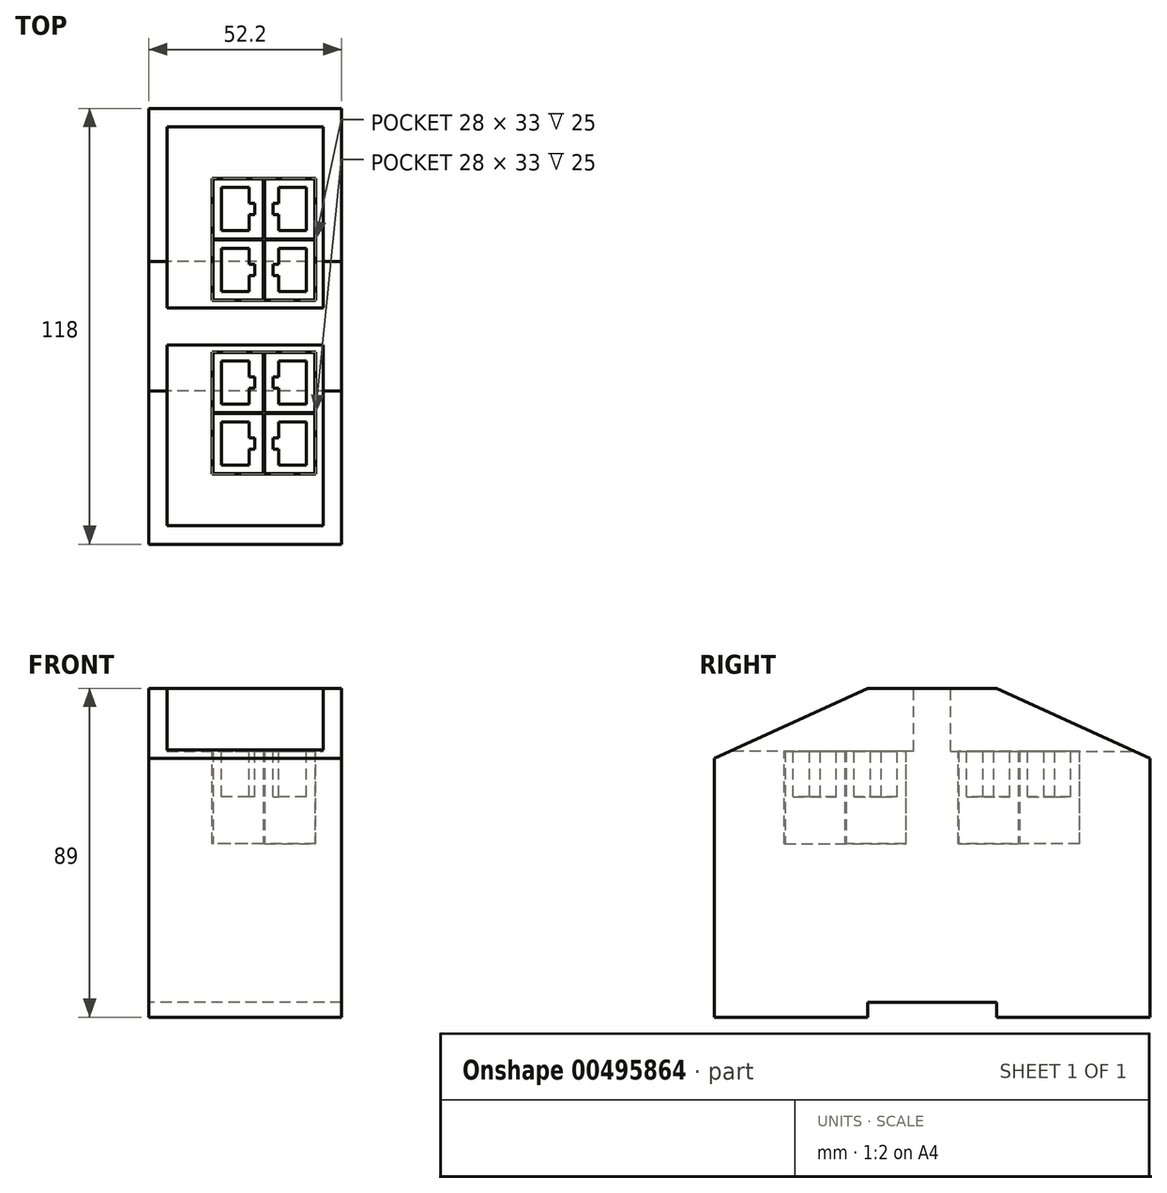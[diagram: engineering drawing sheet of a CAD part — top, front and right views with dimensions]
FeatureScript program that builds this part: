
annotation { "Feature Type Name" : "Feature", "Feature Type Description" : "" }
export const myFeature = defineFeature(function(context is Context, id is Id, definition is map)
    precondition{}
    {
        {
            var Q0;
            Q0=qCreatedBy(makeId("Right.planeOp"),FACE);
            var sketch = newSketch(context, id + "F0", { "sketchPlane" : qUnion([Q0])});
            skLineSegment(sketch, "E0", {"start": v(-59, -4) * mm, "end": v(-17.5, -4) * mm});
            skLineSegment(sketch, "E1", {"start": v(-17.5, -4) * mm, "end": v(-17.5, 0) * mm});
            skLineSegment(sketch, "E2", {"start": v(-17.5, 0) * mm, "end": v(17.5, 0) * mm});
            skLineSegment(sketch, "E3", {"start": v(17.5, 0) * mm, "end": v(17.5, -4) * mm});
            skLineSegment(sketch, "E4", {"start": v(17.5, -4) * mm, "end": v(59, -4) * mm});
            skLineSegment(sketch, "E5", {"start": v(59, -4) * mm, "end": v(59, 66) * mm});
            skLineSegment(sketch, "E6", {"start": v(59, 66) * mm, "end": v(17.5, 85) * mm});
            skLineSegment(sketch, "E7", {"start": v(17.5, 85) * mm, "end": v(-17.5, 85) * mm});
            skLineSegment(sketch, "E8", {"start": v(-17.5, 85) * mm, "end": v(-59, 66) * mm});
            skLineSegment(sketch, "E9", {"start": v(-59, 66) * mm, "end": v(-59, -4) * mm});
            skSolve(sketch);
        }
        {
            var Q0;
            Q0=qSketchRegion(id+"F0",true);
            extrude(context, id + "F1", {"entities" : qUnion([Q0]), "endBound" : BoundingType.SYMMETRIC, "depth" : 52.2 * mm});
        }
        {
            var Q0;
            Q0=makeQuery(id+"F1.opExtrude","SWEPT_FACE",FACE,{"disambiguationData":[OSD([sQuery(id+"F0.wireOp",EDGE,"E7")])]});
            var sketch = newSketch(context, id + "F2", { "sketchPlane" : qUnion([Q0])});
            skLineSegment(sketch, "E10.bottom", {"start": v(-21.1, -5) * mm, "end": v(21.1, -5) * mm});
            skLineSegment(sketch, "E10.top", {"start": v(-21.1, -54) * mm, "end": v(21.1, -54) * mm});
            skLineSegment(sketch, "E10.left", {"start": v(-21.1, -5) * mm, "end": v(-21.1, -54) * mm});
            skLineSegment(sketch, "E10.right", {"start": v(21.1, -5) * mm, "end": v(21.1, -54) * mm});
            skLineSegment(sketch, "E11.MirrorCS", {"start": v(-21.1, 5) * mm, "end": v(21.1, 5) * mm});
            skLineSegment(sketch, "E12.MirrorCS", {"start": v(21.1, 5) * mm, "end": v(21.1, 54) * mm});
            skLineSegment(sketch, "E13.MirrorCS", {"start": v(-21.1, 5) * mm, "end": v(-21.1, 54) * mm});
            skLineSegment(sketch, "E14.MirrorCS", {"start": v(-21.1, 54) * mm, "end": v(21.1, 54) * mm});
            skSolve(sketch);
        }
        {
            var Q0;
            Q0=qSketchRegion(id+"F2",true);
            extrude(context, id + "F3", {"entities" : qUnion([Q0]), "operationType" : NewBodyOperationType.REMOVE, "oppositeDirection" : true, "depth" : 17 * mm});
        }
        {
            var Q0;
            Q0=makeQuery(id+"F3.boolean.opBoolean","COPY",FACE,{"derivedFrom":makeQuery(id+"F3.opExtrude","CAP_FACE",FACE,{"disambiguationData":[OSD([sQuery(id+"F2.wireOp",EDGE,"E10.bottom"),sQuery(id+"F2.wireOp",EDGE,"E10.top"),sQuery(id+"F2.wireOp",EDGE,"E10.left"),sQuery(id+"F2.wireOp",EDGE,"E10.right")])],"isStart":false})});
            var sketch = newSketch(context, id + "F4", { "sketchPlane" : qUnion([Q0])});
            skLineSegment(sketch, "E15.bottom", {"start": v(19.1, -40) * mm, "end": v(-8.9, -40) * mm});
            skLineSegment(sketch, "E15.top", {"start": v(19.1, -7) * mm, "end": v(-8.9, -7) * mm});
            skLineSegment(sketch, "E15.left", {"start": v(19.1, -40) * mm, "end": v(19.1, -7) * mm});
            skLineSegment(sketch, "E15.right", {"start": v(-8.9, -40) * mm, "end": v(-8.9, -7) * mm});
            skLineSegment(sketch, "E16.MirrorCS", {"start": v(-8.9, 40) * mm, "end": v(-8.9, 7) * mm});
            skLineSegment(sketch, "E17.MirrorCS", {"start": v(19.1, 7) * mm, "end": v(-8.9, 7) * mm});
            skLineSegment(sketch, "E18.MirrorCS", {"start": v(19.1, 40) * mm, "end": v(-8.9, 40) * mm});
            skLineSegment(sketch, "E19.MirrorCS", {"start": v(19.1, 40) * mm, "end": v(19.1, 7) * mm});
            skSolve(sketch);
        }
        {
            var Q0;
            Q0=qSketchRegion(id+"F4",true);
            extrude(context, id + "F5", {"entities" : qUnion([Q0]), "operationType" : NewBodyOperationType.REMOVE, "oppositeDirection" : true, "depth" : 25 * mm});
        }
        {
            var Q0;
            Q0=makeQuery(id+"F5.boolean.opBoolean","COPY",FACE,{"derivedFrom":makeQuery(id+"F5.opExtrude","CAP_FACE",FACE,{"disambiguationData":[OSD([sQuery(id+"F4.wireOp",EDGE,"E15.bottom"),sQuery(id+"F4.wireOp",EDGE,"E15.top"),sQuery(id+"F4.wireOp",EDGE,"E15.left"),sQuery(id+"F4.wireOp",EDGE,"E15.right")])],"isStart":false})});
            var sketch = newSketch(context, id + "F6", { "sketchPlane" : qUnion([Q0])});
            skLineSegment(sketch, "E20", {"start": v(5.1, -40) * mm, "end": v(5.1, -7) * mm, "construction": true});
            skLineSegment(sketch, "E21", {"start": v(19.1, -23.5) * mm, "end": v(-8.9, -23.5) * mm, "construction": true});
            skLineSegment(sketch, "E22", {"start": v(5.1, -40) * mm, "end": v(19.1, -23.5) * mm, "construction": true});
            skLineSegment(sketch, "E23", {"start": v(19.1, -23.5) * mm, "end": v(5.1, -7) * mm, "construction": true});
            skLineSegment(sketch, "E24", {"start": v(5.1, -7) * mm, "end": v(-8.9, -23.5) * mm, "construction": true});
            skLineSegment(sketch, "E25", {"start": v(-8.9, -23.5) * mm, "end": v(5.1, -40) * mm, "construction": true});
            skLineSegment(sketch, "E26", {"start": v(-8.9, -40) * mm, "end": v(19.1, -7) * mm, "construction": true});
            skLineSegment(sketch, "E27", {"start": v(19.1, -40) * mm, "end": v(-8.9, -7) * mm, "construction": true});
            skLineSegment(sketch, "E28.bottom", {"start": v(5.35, -39.85) * mm, "end": v(18.85, -39.85) * mm});
            skLineSegment(sketch, "E28.top", {"start": v(5.35, -23.65) * mm, "end": v(18.85, -23.65) * mm});
            skLineSegment(sketch, "E28.left", {"start": v(5.35, -39.85) * mm, "end": v(5.35, -23.65) * mm});
            skLineSegment(sketch, "E28.right", {"start": v(18.85, -39.85) * mm, "end": v(18.85, -23.65) * mm});
            skPoint(sketch, "E28.middle", {"position": v(12.1, -31.75) * mm});
            skLineSegment(sketch, "E29.MirrorCS", {"start": v(4.85, -23.65) * mm, "end": v(-8.65, -23.65) * mm});
            skLineSegment(sketch, "E30.MirrorCS", {"start": v(4.85, -39.85) * mm, "end": v(4.85, -23.65) * mm});
            skLineSegment(sketch, "E31.MirrorCS", {"start": v(4.85, -39.85) * mm, "end": v(-8.65, -39.85) * mm});
            skLineSegment(sketch, "E32.MirrorCS", {"start": v(-8.65, -39.85) * mm, "end": v(-8.65, -23.65) * mm});
            skLineSegment(sketch, "E33.MirrorCS", {"start": v(4.85, -23.35) * mm, "end": v(-8.65, -23.35) * mm});
            skLineSegment(sketch, "E34.MirrorCS", {"start": v(-8.65, -7.15) * mm, "end": v(-8.65, -23.35) * mm});
            skLineSegment(sketch, "E35.MirrorCS", {"start": v(4.85, -7.15) * mm, "end": v(-8.65, -7.15) * mm});
            skLineSegment(sketch, "E36.MirrorCS", {"start": v(4.85, -7.15) * mm, "end": v(4.85, -23.35) * mm});
            skLineSegment(sketch, "E37.MirrorCS", {"start": v(5.35, -7.15) * mm, "end": v(5.35, -23.35) * mm});
            skLineSegment(sketch, "E38.MirrorCS", {"start": v(5.35, -23.35) * mm, "end": v(18.85, -23.35) * mm});
            skLineSegment(sketch, "E39.MirrorCS", {"start": v(5.35, -7.15) * mm, "end": v(18.85, -7.15) * mm});
            skLineSegment(sketch, "E40.MirrorCS", {"start": v(18.85, -7.15) * mm, "end": v(18.85, -23.35) * mm});
            skLineSegment(sketch, "E41.MirrorCS", {"start": v(4.85, 7.15) * mm, "end": v(-8.65, 7.15) * mm});
            skLineSegment(sketch, "E42.MirrorCS", {"start": v(-8.65, 7.15) * mm, "end": v(-8.65, 23.35) * mm});
            skLineSegment(sketch, "E43.MirrorCS", {"start": v(4.85, 23.35) * mm, "end": v(-8.65, 23.35) * mm});
            skLineSegment(sketch, "E44.MirrorCS", {"start": v(4.85, 7.15) * mm, "end": v(4.85, 23.35) * mm});
            skLineSegment(sketch, "E45.MirrorCS", {"start": v(5.35, 7.15) * mm, "end": v(5.35, 23.35) * mm});
            skLineSegment(sketch, "E46.MirrorCS", {"start": v(5.35, 7.15) * mm, "end": v(18.85, 7.15) * mm});
            skLineSegment(sketch, "E47.MirrorCS", {"start": v(18.85, 7.15) * mm, "end": v(18.85, 23.35) * mm});
            skLineSegment(sketch, "E48.MirrorCS", {"start": v(5.35, 23.35) * mm, "end": v(18.85, 23.35) * mm});
            skLineSegment(sketch, "E49.MirrorCS", {"start": v(4.85, 23.65) * mm, "end": v(-8.65, 23.65) * mm});
            skLineSegment(sketch, "E50.MirrorCS", {"start": v(-8.65, 39.85) * mm, "end": v(-8.65, 23.65) * mm});
            skLineSegment(sketch, "E51.MirrorCS", {"start": v(4.85, 39.85) * mm, "end": v(-8.65, 39.85) * mm});
            skLineSegment(sketch, "E52.MirrorCS", {"start": v(4.85, 39.85) * mm, "end": v(4.85, 23.65) * mm});
            skLineSegment(sketch, "E53.MirrorCS", {"start": v(5.35, 39.85) * mm, "end": v(5.35, 23.65) * mm});
            skLineSegment(sketch, "E54.MirrorCS", {"start": v(5.35, 23.65) * mm, "end": v(18.85, 23.65) * mm});
            skLineSegment(sketch, "E55.MirrorCS", {"start": v(5.35, 39.85) * mm, "end": v(18.85, 39.85) * mm});
            skLineSegment(sketch, "E56.MirrorCS", {"start": v(18.85, 39.85) * mm, "end": v(18.85, 23.65) * mm});
            skSolve(sketch);
        }
        {
            var Q0;
            Q0=qSketchRegion(id+"F6",true);
            extrude(context, id + "F7", {"entities" : qUnion([Q0]), "depth" : 25 * mm});
        }
        {
            var Q0;
            Q0=makeQuery(id+"F7.opExtrude","CAP_FACE",FACE,{"disambiguationData":[OSD([sQuery(id+"F6.wireOp",EDGE,"E28.bottom"),sQuery(id+"F6.wireOp",EDGE,"E28.top"),sQuery(id+"F6.wireOp",EDGE,"E28.left"),sQuery(id+"F6.wireOp",EDGE,"E28.right")])],"isStart":false});
            var sketch = newSketch(context, id + "F8", { "sketchPlane" : qUnion([Q0])});
            skLineSegment(sketch, "E57", {"start": v(18.85, -31.75) * mm, "end": v(5.35, -31.75) * mm, "construction": true});
            skLineSegment(sketch, "E58", {"start": v(16.6, -37.6) * mm, "end": v(16.6, -25.91) * mm});
            skLineSegment(sketch, "E59", {"start": v(16.6, -25.91) * mm, "end": v(9.13, -25.91) * mm});
            skLineSegment(sketch, "E60", {"start": v(9.13, -25.91) * mm, "end": v(9.13, -30.25) * mm});
            skLineSegment(sketch, "E61", {"start": v(9.13, -30.25) * mm, "end": v(7.63, -30.25) * mm});
            skLineSegment(sketch, "E62", {"start": v(7.63, -30.25) * mm, "end": v(7.63, -33.25) * mm});
            skLineSegment(sketch, "E63", {"start": v(7.63, -33.25) * mm, "end": v(9.13, -33.25) * mm});
            skLineSegment(sketch, "E64", {"start": v(9.13, -33.25) * mm, "end": v(9.13, -37.6) * mm});
            skLineSegment(sketch, "E65", {"start": v(9.13, -37.6) * mm, "end": v(16.6, -37.6) * mm});
            skPoint(sketch, "E66.0", {"position": v(5.1, -40) * mm});
            skPoint(sketch, "E67.0", {"position": v(19.1, -23.5) * mm});
            skLineSegment(sketch, "E68", {"start": v(5.1, -40) * mm, "end": v(5.1, -5.87) * mm, "construction": true});
            skLineSegment(sketch, "E69", {"start": v(19.1, -23.5) * mm, "end": v(-9.98, -23.5) * mm, "construction": true});
            skLineSegment(sketch, "E70.MirrorCS", {"start": v(1.07, -33.25) * mm, "end": v(1.07, -37.6) * mm});
            skLineSegment(sketch, "E71.MirrorCS", {"start": v(2.57, -33.25) * mm, "end": v(1.07, -33.25) * mm});
            skLineSegment(sketch, "E72.MirrorCS", {"start": v(2.57, -30.25) * mm, "end": v(2.57, -33.25) * mm});
            skLineSegment(sketch, "E73.MirrorCS", {"start": v(1.07, -30.25) * mm, "end": v(2.57, -30.25) * mm});
            skLineSegment(sketch, "E74.MirrorCS", {"start": v(1.07, -25.91) * mm, "end": v(1.07, -30.25) * mm});
            skLineSegment(sketch, "E75.MirrorCS", {"start": v(-6.4, -25.91) * mm, "end": v(1.07, -25.91) * mm});
            skLineSegment(sketch, "E76.MirrorCS", {"start": v(1.07, -37.6) * mm, "end": v(-6.4, -37.6) * mm});
            skLineSegment(sketch, "E77.MirrorCS", {"start": v(-6.4, -37.6) * mm, "end": v(-6.4, -25.91) * mm});
            skLineSegment(sketch, "E78.MirrorCS", {"start": v(1.07, -13.75) * mm, "end": v(1.07, -9.4) * mm});
            skLineSegment(sketch, "E79.MirrorCS", {"start": v(1.07, -9.4) * mm, "end": v(-6.4, -9.4) * mm});
            skLineSegment(sketch, "E80.MirrorCS", {"start": v(-6.4, -9.4) * mm, "end": v(-6.4, -21.09) * mm});
            skLineSegment(sketch, "E81.MirrorCS", {"start": v(-6.4, -21.09) * mm, "end": v(1.07, -21.09) * mm});
            skLineSegment(sketch, "E82.MirrorCS", {"start": v(1.07, -21.09) * mm, "end": v(1.07, -16.75) * mm});
            skLineSegment(sketch, "E83.MirrorCS", {"start": v(1.07, -16.75) * mm, "end": v(2.57, -16.75) * mm});
            skLineSegment(sketch, "E84.MirrorCS", {"start": v(2.57, -16.75) * mm, "end": v(2.57, -13.75) * mm});
            skLineSegment(sketch, "E85.MirrorCS", {"start": v(2.57, -13.75) * mm, "end": v(1.07, -13.75) * mm});
            skLineSegment(sketch, "E86.MirrorCS", {"start": v(9.13, -13.75) * mm, "end": v(9.13, -9.4) * mm});
            skLineSegment(sketch, "E87.MirrorCS", {"start": v(7.63, -13.75) * mm, "end": v(9.13, -13.75) * mm});
            skLineSegment(sketch, "E88.MirrorCS", {"start": v(7.63, -16.75) * mm, "end": v(7.63, -13.75) * mm});
            skLineSegment(sketch, "E89.MirrorCS", {"start": v(9.13, -16.75) * mm, "end": v(7.63, -16.75) * mm});
            skLineSegment(sketch, "E90.MirrorCS", {"start": v(9.13, -21.09) * mm, "end": v(9.13, -16.75) * mm});
            skLineSegment(sketch, "E91.MirrorCS", {"start": v(16.6, -21.09) * mm, "end": v(9.13, -21.09) * mm});
            skLineSegment(sketch, "E92.MirrorCS", {"start": v(9.13, -9.4) * mm, "end": v(16.6, -9.4) * mm});
            skLineSegment(sketch, "E93.MirrorCS", {"start": v(16.6, -9.4) * mm, "end": v(16.6, -21.09) * mm});
            skLineSegment(sketch, "E94.MirrorCS", {"start": v(-6.4, 21.09) * mm, "end": v(1.07, 21.09) * mm});
            skLineSegment(sketch, "E95.MirrorCS", {"start": v(-6.4, 9.4) * mm, "end": v(-6.4, 21.09) * mm});
            skLineSegment(sketch, "E96.MirrorCS", {"start": v(1.07, 9.4) * mm, "end": v(-6.4, 9.4) * mm});
            skLineSegment(sketch, "E97.MirrorCS", {"start": v(1.07, 13.75) * mm, "end": v(1.07, 9.41) * mm});
            skLineSegment(sketch, "E98.MirrorCS", {"start": v(2.57, 13.75) * mm, "end": v(1.07, 13.75) * mm});
            skLineSegment(sketch, "E99.MirrorCS", {"start": v(2.57, 16.75) * mm, "end": v(2.57, 13.75) * mm});
            skLineSegment(sketch, "E100.MirrorCS", {"start": v(1.07, 16.75) * mm, "end": v(2.57, 16.75) * mm});
            skLineSegment(sketch, "E101.MirrorCS", {"start": v(1.07, 21.09) * mm, "end": v(1.07, 16.75) * mm});
            skLineSegment(sketch, "E102.MirrorCS", {"start": v(9.13, 21.09) * mm, "end": v(9.13, 16.75) * mm});
            skLineSegment(sketch, "E103.MirrorCS", {"start": v(9.13, 16.75) * mm, "end": v(7.63, 16.75) * mm});
            skLineSegment(sketch, "E104.MirrorCS", {"start": v(7.63, 16.75) * mm, "end": v(7.63, 13.75) * mm});
            skLineSegment(sketch, "E105.MirrorCS", {"start": v(7.63, 13.75) * mm, "end": v(9.13, 13.75) * mm});
            skLineSegment(sketch, "E106.MirrorCS", {"start": v(9.13, 13.75) * mm, "end": v(9.13, 9.41) * mm});
            skLineSegment(sketch, "E107.MirrorCS", {"start": v(9.13, 9.41) * mm, "end": v(16.6, 9.41) * mm});
            skLineSegment(sketch, "E108.MirrorCS", {"start": v(16.6, 9.41) * mm, "end": v(16.6, 21.09) * mm});
            skLineSegment(sketch, "E109.MirrorCS", {"start": v(16.6, 21.09) * mm, "end": v(9.13, 21.09) * mm});
            skLineSegment(sketch, "E110.MirrorCS", {"start": v(1.07, 33.25) * mm, "end": v(1.07, 37.6) * mm});
            skLineSegment(sketch, "E111.MirrorCS", {"start": v(1.07, 37.6) * mm, "end": v(-6.4, 37.6) * mm});
            skLineSegment(sketch, "E112.MirrorCS", {"start": v(-6.4, 37.6) * mm, "end": v(-6.4, 25.91) * mm});
            skLineSegment(sketch, "E113.MirrorCS", {"start": v(-6.4, 25.91) * mm, "end": v(1.07, 25.91) * mm});
            skLineSegment(sketch, "E114.MirrorCS", {"start": v(1.07, 25.91) * mm, "end": v(1.07, 30.25) * mm});
            skLineSegment(sketch, "E115.MirrorCS", {"start": v(1.07, 30.25) * mm, "end": v(2.57, 30.25) * mm});
            skLineSegment(sketch, "E116.MirrorCS", {"start": v(2.57, 30.25) * mm, "end": v(2.57, 33.25) * mm});
            skLineSegment(sketch, "E117.MirrorCS", {"start": v(2.57, 33.25) * mm, "end": v(1.07, 33.25) * mm});
            skLineSegment(sketch, "E118.MirrorCS", {"start": v(9.13, 33.25) * mm, "end": v(9.13, 37.6) * mm});
            skLineSegment(sketch, "E119.MirrorCS", {"start": v(7.63, 33.25) * mm, "end": v(9.13, 33.25) * mm});
            skLineSegment(sketch, "E120.MirrorCS", {"start": v(7.63, 30.25) * mm, "end": v(7.63, 33.25) * mm});
            skLineSegment(sketch, "E121.MirrorCS", {"start": v(9.13, 30.25) * mm, "end": v(7.63, 30.25) * mm});
            skLineSegment(sketch, "E122.MirrorCS", {"start": v(9.13, 25.91) * mm, "end": v(9.13, 30.25) * mm});
            skLineSegment(sketch, "E123.MirrorCS", {"start": v(16.6, 25.91) * mm, "end": v(9.13, 25.91) * mm});
            skLineSegment(sketch, "E124.MirrorCS", {"start": v(9.13, 37.6) * mm, "end": v(16.6, 37.6) * mm});
            skLineSegment(sketch, "E125.MirrorCS", {"start": v(16.6, 37.6) * mm, "end": v(16.6, 25.91) * mm});
            skSolve(sketch);
        }
        {
            var Q0;
            Q0=qSketchRegion(id+"F8",true);
            extrude(context, id + "F9", {"entities" : qUnion([Q0]), "operationType" : NewBodyOperationType.REMOVE, "oppositeDirection" : true, "depth" : 12.32 * mm});
        }
    });
